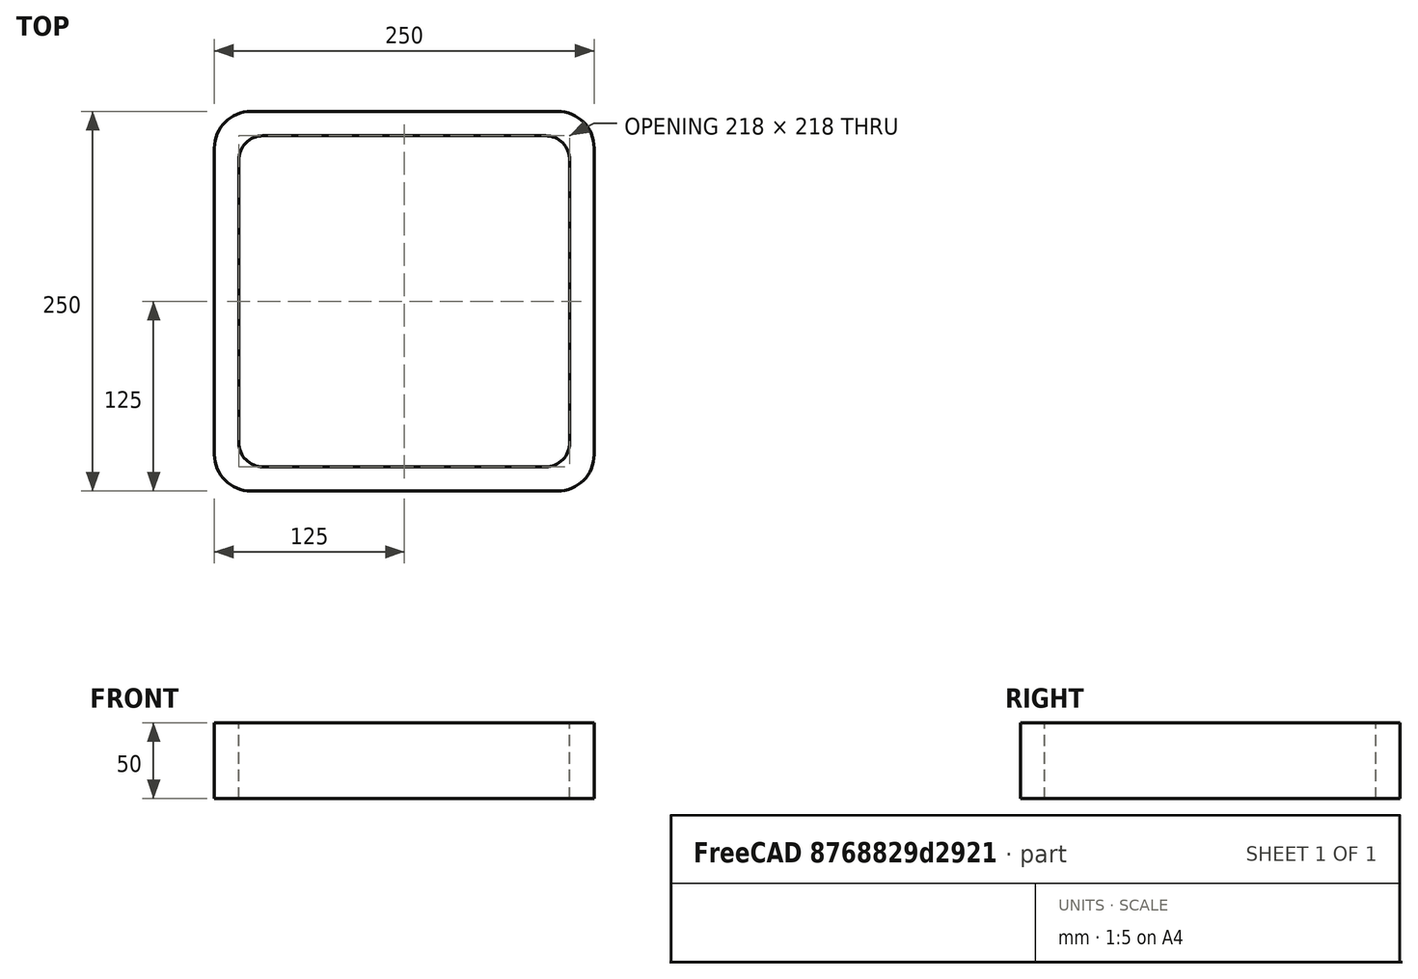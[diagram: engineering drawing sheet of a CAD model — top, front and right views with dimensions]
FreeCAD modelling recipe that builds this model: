
FCSTD DOCUMENT  (FreeCAD 0.15R4671 (Git))
Label: Square hollow section 250x250x16 EN10219 S235JRH
License: All rights reserved
LicenseURL: http://en.wikipedia.org/wiki/All_rights_reserved
objects: Sketcher::SketchObject×1, Part::Extrusion×1
note: 2 computed .brp shape members not serialized (recipe doc carries the construction recipe); baked Part::Feature solids carry a one-line shape summary decoded from their .brp

FEATURE [Sketcher::SketchObject] Sketch
  sketch-geometry (16):
    g0: LineSegment StartX=-93 StartY=109 StartZ=0 EndX=93 EndY=109 EndZ=0
    g1: LineSegment StartX=109 StartY=93 StartZ=0 EndX=109 EndY=-93 EndZ=0
    g2: LineSegment StartX=93 StartY=-109 StartZ=0 EndX=-93 EndY=-109 EndZ=0
    g3: LineSegment StartX=-109 StartY=-93 StartZ=0 EndX=-109 EndY=93 EndZ=0
    g4: LineSegment StartX=-101 StartY=125 StartZ=0 EndX=101 EndY=125 EndZ=0
    g5: LineSegment StartX=125 StartY=101 StartZ=0 EndX=125 EndY=-101 EndZ=0
    g6: LineSegment StartX=101 StartY=-125 StartZ=0 EndX=-101 EndY=-125 EndZ=0
    g7: LineSegment StartX=-125 StartY=-101 StartZ=0 EndX=-125 EndY=101 EndZ=0
    g8: ArcOfCircle CenterX=-93 CenterY=93 CenterZ=0 NormalX=0 NormalY=0 NormalZ=1 Radius=16 StartAngle=1.5708 EndAngle=3.14159
    g9: ArcOfCircle CenterX=93 CenterY=93 CenterZ=0 NormalX=0 NormalY=0 NormalZ=1 Radius=16 StartAngle=0 EndAngle=1.5708
    g10: ArcOfCircle CenterX=93 CenterY=-93 CenterZ=0 NormalX=0 NormalY=0 NormalZ=1 Radius=16 StartAngle=4.71239 EndAngle=6.28319
    g11: ArcOfCircle CenterX=-93 CenterY=-93 CenterZ=0 NormalX=0 NormalY=0 NormalZ=1 Radius=16 StartAngle=3.14159 EndAngle=4.71239
    g12: ArcOfCircle CenterX=101 CenterY=101 CenterZ=0 NormalX=0 NormalY=0 NormalZ=1 Radius=24 StartAngle=0 EndAngle=1.5708
    g13: ArcOfCircle CenterX=101 CenterY=-101 CenterZ=0 NormalX=0 NormalY=0 NormalZ=1 Radius=24 StartAngle=4.71239 EndAngle=6.28319
    g14: ArcOfCircle CenterX=-101 CenterY=-101 CenterZ=0 NormalX=0 NormalY=0 NormalZ=1 Radius=24 StartAngle=3.14159 EndAngle=4.71239
    g15: ArcOfCircle CenterX=-101 CenterY=101 CenterZ=0 NormalX=0 NormalY=0 NormalZ=1 Radius=24 StartAngle=1.5708 EndAngle=3.14159
  constraints (36):
    c: Horizontal(g2)
    c: Vertical(g3)
    c: Horizontal(g6)
    c: Vertical(g7)
    c: Tangent(g3,g8) = 1.5708
    c: Tangent(g0,g8) = 1.5708
    c: Tangent(g0,g9) = 1.5708
    c: Tangent(g1,g9) = 1.5708
    c: Tangent(g1,g10) = 1.5708
    c: Tangent(g2,g10) = 1.5708
    c: Tangent(g2,g11) = 1.5708
    c: Tangent(g3,g11) = 1.5708
    c: Tangent(g4,g12) = 1.5708
    c: Tangent(g5,g12) = 1.5708
    c: Tangent(g5,g13) = 1.5708
    c: Tangent(g6,g13) = 1.5708
    c: Tangent(g6,g14) = 1.5708
    c: Tangent(g7,g14) = 1.5708
    c: Tangent(g7,g15) = 1.5708
    c: Tangent(g4,g15) = 1.5708
    c: Equal(g9,g8)
    c: Equal(g9,g11)
    c: Equal(g9,g10)
    c: Equal(g12,g15)
    c: Equal(g12,g14)
    c: Equal(g12,g13)
    c: Symmetric(g4,g6,g-1)
    c: Symmetric(g7,g5,g-2)
    c: DistanceY(g4,g6) = -250
    c: DistanceX(g7,g5) = 250
    c: Symmetric(g3,g1,g-2)
    c: Symmetric(g0,g2,g-1)
    c: DistanceY(g0,g4) = 16
    c: DistanceX(g5,g1) = -16
    c: Radius(g9) = 16
    c: Radius(g12) = 24
FEATURE [Part::Extrusion] Extrude  label="Square hollow section 250x250x16 EN10219 S235JRH"
  Base = -> Sketch
  Dir = (0,0,50)
  Solid = true
